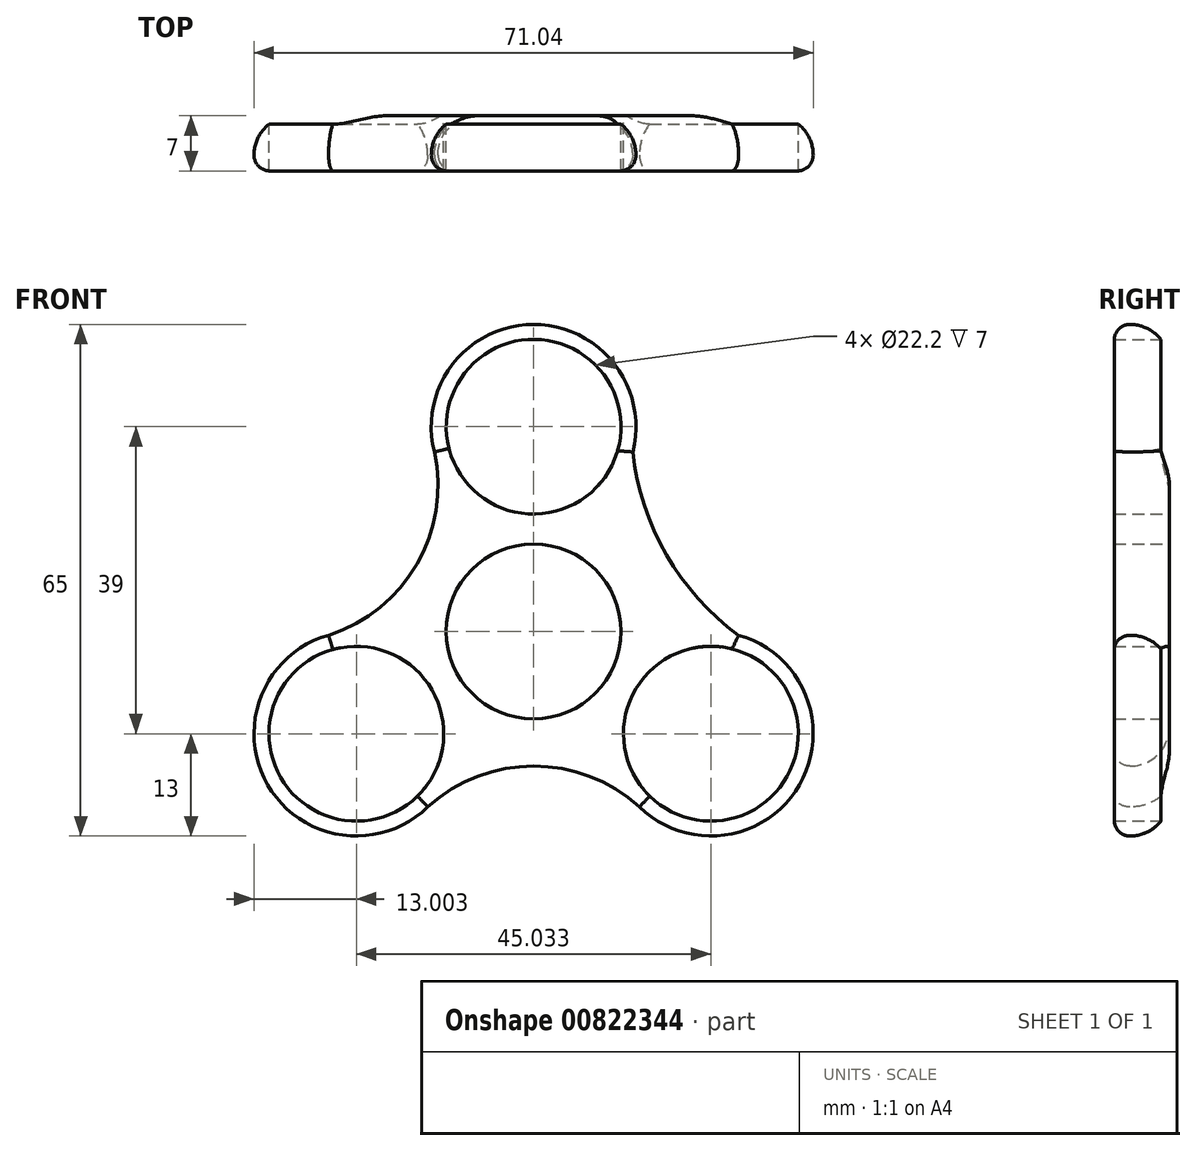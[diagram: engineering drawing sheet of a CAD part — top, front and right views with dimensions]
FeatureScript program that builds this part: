
annotation { "Feature Type Name" : "Feature", "Feature Type Description" : "" }
export const myFeature = defineFeature(function(context is Context, id is Id, definition is map)
    precondition{}
    {
        {
            var Q0;
            Q0=qCreatedBy(makeId("Front.planeOp"),FACE);
            var sketch = newSketch(context, id + "F0", { "sketchPlane" : qUnion([Q0]), "disableImprinting" : false});
            skCircle(sketch, "E0", {"center": v(0, 0) * mm, "radius": 11.1 * mm});
            skCircle(sketch, "E1", {"center": v(0, 26) * mm, "radius": 11.1 * mm});
            skCircle(sketch, "E2.1.0", {"center": v(-22.52, -13) * mm, "radius": 11.1 * mm});
            skCircle(sketch, "E2.2.0", {"center": v(22.52, -13) * mm, "radius": 11.1 * mm});
            skArc(sketch, "E3", {"start": v(12.6, 22.8) * mm, "mid": v(0, 39) * mm, "end": v(-12.6, 22.8) * mm});
            skArc(sketch, "E4", {"start": v(-26.04, -0.49) * mm, "mid": v(-33.77, -19.5) * mm, "end": v(-13.44, -22.31) * mm});
            skArc(sketch, "E5", {"start": v(13.44, -22.31) * mm, "mid": v(33.77, -19.5) * mm, "end": v(26.04, -0.49) * mm});
            skArc(sketch, "E6", {"start": v(13.44, -22.31) * mm, "mid": v(0, -17.12) * mm, "end": v(-13.44, -22.31) * mm});
            skArc(sketch, "E7", {"start": v(-26.04, -0.49) * mm, "mid": v(-14.82, 8.56) * mm, "end": v(-12.6, 22.8) * mm});
            skArc(sketch, "E8", {"start": v(12.6, 22.8) * mm, "mid": v(16.86, 9.73) * mm, "end": v(26.04, -0.49) * mm});
            skSolve(sketch);
        }
        {
            var Q0;
            Q0 = qSketchRegion(id + "F0", true);
            extrude(context, id + "F1", {"entities" : qUnion([Q0]), "flatOperationType" : FlatOperationType.REMOVE, "depth" : 7 * mm, "offsetDistance" : 25 * mm, "domain" : OperationDomain.MODEL});
        }
        {
            var Q0;
            Q0=makeQuery(id+"F1.opExtrude","CAP_EDGE",EDGE,{"disambiguationData":[OSD([sQuery(id+"F0.wireOp",EDGE,"E7")])],"isStart":false});
            var Q1;
            Q1=makeQuery(id+"F1.opExtrude","CAP_EDGE",EDGE,{"disambiguationData":[OSD([sQuery(id+"F0.wireOp",EDGE,"E3")])],"isStart":false});
            var Q2;
            Q2=makeQuery(id+"F1.opExtrude","CAP_EDGE",EDGE,{"disambiguationData":[OSD([sQuery(id+"F0.wireOp",EDGE,"E8")])],"isStart":false});
            var Q3;
            Q3=makeQuery(id+"F1.opExtrude","CAP_EDGE",EDGE,{"disambiguationData":[OSD([sQuery(id+"F0.wireOp",EDGE,"E5")])],"isStart":false});
            var Q4;
            Q4=makeQuery(id+"F1.opExtrude","CAP_EDGE",EDGE,{"disambiguationData":[OSD([sQuery(id+"F0.wireOp",EDGE,"E6")])],"isStart":false});
            var Q5;
            Q5=makeQuery(id+"F1.opExtrude","CAP_EDGE",EDGE,{"disambiguationData":[OSD([sQuery(id+"F0.wireOp",EDGE,"E4")])],"isStart":false});
            fillet(context, id + "F2", {"entities" : qUnion([Q0, Q1, Q2, Q3, Q4, Q5]), "radius" : 2 * mm, "tangentPropagation" : true, "allowEdgeOverflow" : false});
        }
        {
            var Q0;
            Q0=makeQuery(id+"F1.opExtrude","CAP_EDGE",EDGE,{"disambiguationData":[OSD([sQuery(id+"F0.wireOp",EDGE,"E5")])],"isStart":true});
            var Q1;
            Q1=makeQuery(id+"F1.opExtrude","CAP_EDGE",EDGE,{"disambiguationData":[OSD([sQuery(id+"F0.wireOp",EDGE,"E8")])],"isStart":true});
            var Q2;
            Q2=makeQuery(id+"F1.opExtrude","CAP_EDGE",EDGE,{"disambiguationData":[OSD([sQuery(id+"F0.wireOp",EDGE,"E3")])],"isStart":true});
            var Q3;
            Q3=makeQuery(id+"F1.opExtrude","CAP_EDGE",EDGE,{"disambiguationData":[OSD([sQuery(id+"F0.wireOp",EDGE,"E7")])],"isStart":true});
            var Q4;
            Q4=makeQuery(id+"F1.opExtrude","CAP_EDGE",EDGE,{"disambiguationData":[OSD([sQuery(id+"F0.wireOp",EDGE,"E4")])],"isStart":true});
            var Q5;
            Q5=makeQuery(id+"F1.opExtrude","CAP_EDGE",EDGE,{"disambiguationData":[OSD([sQuery(id+"F0.wireOp",EDGE,"E6")])],"isStart":true});
            fillet(context, id + "F3", {"entities" : qUnion([Q0, Q1, Q2, Q3, Q4, Q5]), "radius" : 5 * mm, "tangentPropagation" : true, "allowEdgeOverflow" : false});
        }
    });
